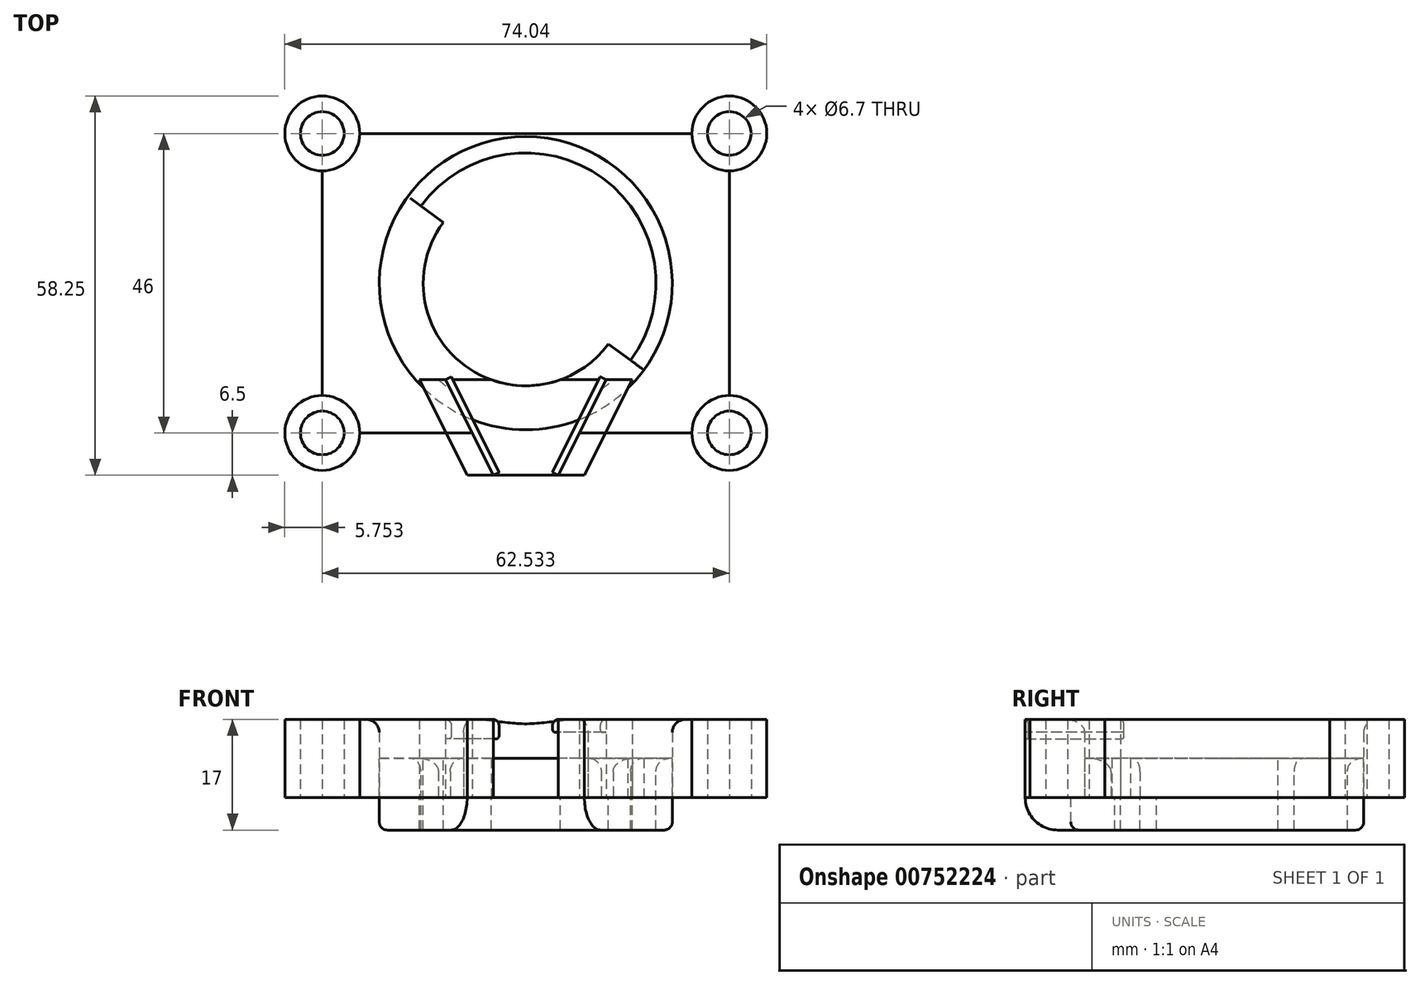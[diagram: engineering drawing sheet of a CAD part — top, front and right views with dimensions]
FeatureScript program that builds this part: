
annotation { "Feature Type Name" : "Feature", "Feature Type Description" : "" }
export const myFeature = defineFeature(function(context is Context, id is Id, definition is map)
    precondition{}
    {
        {
            var Q0;
            Q0=qCreatedBy(makeId("Top.planeOp"),FACE);
            var sketch = newSketch(context, id + "F0", { "sketchPlane" : qUnion([Q0])});
            skCircle(sketch, "E0", {"center": v(-31.27, 23) * mm, "radius": 5.75 * mm});
            skCircle(sketch, "E1", {"center": v(31.27, -23) * mm, "radius": 5.75 * mm});
            skCircle(sketch, "E2", {"center": v(31.27, -23) * mm, "radius": 3.35 * mm});
            skCircle(sketch, "E3", {"center": v(-31.27, 23) * mm, "radius": 3.35 * mm});
            skLineSegment(sketch, "E4", {"start": v(-31.27, 23) * mm, "end": v(31.27, -23) * mm});
            skCircle(sketch, "E5", {"center": v(0, 0) * mm, "radius": 20 * mm});
            skCircle(sketch, "E6", {"center": v(0, 0) * mm, "radius": 15.75 * mm});
            skLineSegment(sketch, "E7", {"start": v(-31.27, 23) * mm, "end": v(-31.27, -23) * mm});
            skLineSegment(sketch, "E8", {"start": v(-31.27, -23) * mm, "end": v(31.27, -23) * mm});
            skCircle(sketch, "E9", {"center": v(-31.27, -23) * mm, "radius": 5.75 * mm});
            skCircle(sketch, "E10", {"center": v(-31.27, -23) * mm, "radius": 3.35 * mm});
            skLineSegment(sketch, "E11", {"start": v(-31.27, 23) * mm, "end": v(31.27, 23) * mm});
            skCircle(sketch, "E12", {"center": v(31.27, 23) * mm, "radius": 5.75 * mm});
            skCircle(sketch, "E13", {"center": v(31.27, 23) * mm, "radius": 3.35 * mm});
            skLineSegment(sketch, "E14", {"start": v(31.27, -23) * mm, "end": v(31.27, 23) * mm});
            skLineSegment(sketch, "E15", {"start": v(0, 0) * mm, "end": v(0, -29.5) * mm});
            skLineSegment(sketch, "E16", {"start": v(-5, -29.5) * mm, "end": v(5, -29.5) * mm});
            skLineSegment(sketch, "E17", {"start": v(-5, -29.5) * mm, "end": v(-9, -29.5) * mm});
            skLineSegment(sketch, "E18", {"start": v(5, -29.5) * mm, "end": v(9, -29.5) * mm});
            skLineSegment(sketch, "E19", {"start": v(-5, -29.5) * mm, "end": v(-12.33, -14.82) * mm});
            skLineSegment(sketch, "E20", {"start": v(-12.33, -14.82) * mm, "end": v(12.33, -14.82) * mm});
            skLineSegment(sketch, "E21", {"start": v(12.33, -14.82) * mm, "end": v(5, -29.5) * mm});
            skLineSegment(sketch, "E22", {"start": v(-12.33, -14.82) * mm, "end": v(-16.33, -14.82) * mm});
            skLineSegment(sketch, "E23", {"start": v(-16.33, -14.82) * mm, "end": v(-9, -29.5) * mm});
            skLineSegment(sketch, "E24", {"start": v(9, -29.5) * mm, "end": v(16.32, -14.82) * mm});
            skLineSegment(sketch, "E25", {"start": v(16.32, -14.82) * mm, "end": v(12.33, -14.82) * mm});
            skCircle(sketch, "E26", {"center": v(0, 0) * mm, "radius": 22.5 * mm});
            skSolve(sketch);
        }
        {
            var Q0;
            {var subQ0=sQuery(id+"F0.wireOp",EDGE,"E9");var subQ1=sQuery(id+"F0.wireOp",EDGE,"E7");var subQ2=makeQuery(id+"F0.imprint","INTERSECT",VERTEX,{"derivedFrom":[subQ1,subQ0]});Q0=makeQuery(id+"F0.imprint","IMPRINT",FACE,{"disambiguationData":[TD([[makeQuery(id+"F0.imprint","IMPRINT",EDGE,{"disambiguationData":[TD([[subQ2,-1.0]])],"derivedFrom":subQ1}),-1.0]])]});}
            var Q1;
            {var subQ0=sQuery(id+"F0.wireOp",EDGE,"E12");var subQ1=sQuery(id+"F0.wireOp",EDGE,"E11");var subQ2=makeQuery(id+"F0.imprint","INTERSECT",VERTEX,{"derivedFrom":[subQ1,subQ0]});Q1=makeQuery(id+"F0.imprint","IMPRINT",FACE,{"disambiguationData":[TD([[makeQuery(id+"F0.imprint","IMPRINT",EDGE,{"disambiguationData":[TD([[subQ2,-1.0]])],"derivedFrom":subQ1}),1.0]])]});}
            var Q2;
            {var subQ0=sQuery(id+"F0.wireOp",EDGE,"E7");var subQ1=sQuery(id+"F0.wireOp",EDGE,"E0");var subQ2=makeQuery(id+"F0.imprint","INTERSECT",VERTEX,{"derivedFrom":[subQ1,subQ0]});Q2=makeQuery(id+"F0.imprint","IMPRINT",FACE,{"disambiguationData":[TD([[makeQuery(id+"F0.imprint","IMPRINT",EDGE,{"disambiguationData":[TD([[subQ2,1.0]])],"derivedFrom":subQ1}),1.0]])]});}
            var Q3;
            {var subQ0=sQuery(id+"F0.wireOp",EDGE,"E14");var subQ1=sQuery(id+"F0.wireOp",EDGE,"E1");var subQ2=makeQuery(id+"F0.imprint","INTERSECT",VERTEX,{"derivedFrom":[subQ1,subQ0]});Q3=makeQuery(id+"F0.imprint","IMPRINT",FACE,{"disambiguationData":[TD([[makeQuery(id+"F0.imprint","IMPRINT",EDGE,{"disambiguationData":[TD([[subQ2,1.0]])],"derivedFrom":subQ1}),1.0]])]});}
            var Q4;
            {var subQ0=sQuery(id+"F0.wireOp",EDGE,"E9");var subQ1=sQuery(id+"F0.wireOp",EDGE,"E7");var subQ2=makeQuery(id+"F0.imprint","INTERSECT",VERTEX,{"derivedFrom":[subQ1,subQ0]});Q4=makeQuery(id+"F0.imprint","IMPRINT",FACE,{"disambiguationData":[TD([[makeQuery(id+"F0.imprint","IMPRINT",EDGE,{"disambiguationData":[TD([[subQ2,-1.0]])],"derivedFrom":subQ1}),1.0]])]});}
            var Q5;
            {var subQ0=sQuery(id+"F0.wireOp",EDGE,"E12");var subQ1=sQuery(id+"F0.wireOp",EDGE,"E11");var subQ2=makeQuery(id+"F0.imprint","INTERSECT",VERTEX,{"derivedFrom":[subQ1,subQ0]});Q5=makeQuery(id+"F0.imprint","IMPRINT",FACE,{"disambiguationData":[TD([[makeQuery(id+"F0.imprint","IMPRINT",EDGE,{"disambiguationData":[TD([[subQ2,-1.0]])],"derivedFrom":subQ1}),-1.0]])]});}
            var Q6;
            {var subQ0=sQuery(id+"F0.wireOp",EDGE,"E7");var subQ1=sQuery(id+"F0.wireOp",EDGE,"E0");var subQ2=makeQuery(id+"F0.imprint","INTERSECT",VERTEX,{"derivedFrom":[subQ1,subQ0]});Q6=makeQuery(id+"F0.imprint","IMPRINT",FACE,{"disambiguationData":[TD([[makeQuery(id+"F0.imprint","IMPRINT",EDGE,{"disambiguationData":[TD([[subQ2,-1.0]])],"derivedFrom":subQ1}),1.0]])]});}
            var Q7;
            {var subQ0=sQuery(id+"F0.wireOp",EDGE,"E11");var subQ1=sQuery(id+"F0.wireOp",EDGE,"E0");var subQ2=makeQuery(id+"F0.imprint","INTERSECT",VERTEX,{"derivedFrom":[subQ1,subQ0]});Q7=makeQuery(id+"F0.imprint","IMPRINT",FACE,{"disambiguationData":[TD([[makeQuery(id+"F0.imprint","IMPRINT",EDGE,{"disambiguationData":[TD([[subQ2,1.0]])],"derivedFrom":subQ1}),1.0]])]});}
            var Q8;
            {var subQ0=sQuery(id+"F0.wireOp",EDGE,"E14");var subQ1=sQuery(id+"F0.wireOp",EDGE,"E1");var subQ2=makeQuery(id+"F0.imprint","INTERSECT",VERTEX,{"derivedFrom":[subQ1,subQ0]});Q8=makeQuery(id+"F0.imprint","IMPRINT",FACE,{"disambiguationData":[TD([[makeQuery(id+"F0.imprint","IMPRINT",EDGE,{"disambiguationData":[TD([[subQ2,-1.0]])],"derivedFrom":subQ1}),1.0]])]});}
            var Q9;
            {var subQ0=sQuery(id+"F0.wireOp",EDGE,"E8");var subQ1=sQuery(id+"F0.wireOp",EDGE,"E1");var subQ2=makeQuery(id+"F0.imprint","INTERSECT",VERTEX,{"derivedFrom":[subQ1,subQ0]});Q9=makeQuery(id+"F0.imprint","IMPRINT",FACE,{"disambiguationData":[TD([[makeQuery(id+"F0.imprint","IMPRINT",EDGE,{"disambiguationData":[TD([[subQ2,1.0]])],"derivedFrom":subQ1}),1.0]])]});}
            extrude(context, id + "F1", {"entities" : qUnion([Q0, Q1, Q2, Q3, Q4, Q5, Q6, Q7, Q8, Q9]), "depth" : 12 * mm, "offsetDistance" : 25 * mm});
        }
        {
            var Q0;
            {var subQ5=sQuery(id+"F0.wireOp",EDGE,"E15");var subQ6=sQuery(id+"F0.wireOp",EDGE,"E5");var subQ7=makeQuery(id+"F0.imprint","INTERSECT",VERTEX,{"derivedFrom":[subQ6,subQ5]});Q0=makeQuery(id+"F0.imprint","IMPRINT",FACE,{"disambiguationData":[TD([[makeQuery(id+"F0.imprint","IMPRINT",EDGE,{"disambiguationData":[TD([[subQ7,-1.0]])],"derivedFrom":subQ6}),1.0]])]});}
            var Q1;
            {var subQ3=sQuery(id+"F0.wireOp",EDGE,"E6");var subQ5=sQuery(id+"F0.wireOp",EDGE,"E4");var subQ6=makeQuery(id+"F0.imprint","INTERSECT",VERTEX,{"disambiguationData":[OD(1.0)],"derivedFrom":[subQ5,subQ3]});Q1=makeQuery(id+"F0.imprint","IMPRINT",FACE,{"disambiguationData":[TD([[makeQuery(id+"F0.imprint","IMPRINT",EDGE,{"disambiguationData":[TD([[subQ6,-1.0]])],"derivedFrom":subQ5}),-1.0]])]});}
            var Q2;
            {var subQ0=sQuery(id+"F0.wireOp",EDGE,"E21");var subQ1=sQuery(id+"F0.wireOp",EDGE,"E5");var subQ2=makeQuery(id+"F0.imprint","INTERSECT",VERTEX,{"derivedFrom":[subQ1,subQ0]});Q2=makeQuery(id+"F0.imprint","IMPRINT",FACE,{"disambiguationData":[TD([[makeQuery(id+"F0.imprint","IMPRINT",EDGE,{"disambiguationData":[TD([[subQ2,-1.0]])],"derivedFrom":subQ1}),1.0]])]});}
            var Q3;
            {var subQ0=sQuery(id+"F0.wireOp",EDGE,"E5");var subQ1=sQuery(id+"F0.wireOp",EDGE,"E4");var subQ2=makeQuery(id+"F0.imprint","INTERSECT",VERTEX,{"disambiguationData":[OD(0.0)],"derivedFrom":[subQ1,subQ0]});Q3=makeQuery(id+"F0.imprint","IMPRINT",FACE,{"disambiguationData":[TD([[makeQuery(id+"F0.imprint","IMPRINT",EDGE,{"disambiguationData":[TD([[subQ2,-1.0]])],"derivedFrom":subQ1}),1.0]])]});}
            var Q4;
            {var subQ5=sQuery(id+"F0.wireOp",EDGE,"E5");var subQ6=sQuery(id+"F0.wireOp",EDGE,"E4");var subQ7=makeQuery(id+"F0.imprint","INTERSECT",VERTEX,{"disambiguationData":[OD(0.0)],"derivedFrom":[subQ6,subQ5]});Q4=makeQuery(id+"F0.imprint","IMPRINT",FACE,{"disambiguationData":[TD([[makeQuery(id+"F0.imprint","IMPRINT",EDGE,{"disambiguationData":[TD([[subQ7,-1.0]])],"derivedFrom":subQ6}),-1.0]])]});}
            var Q5;
            {var subQ1=sQuery(id+"F0.wireOp",EDGE,"E19");var subQ3=sQuery(id+"F0.wireOp",EDGE,"E5");var subQ4=makeQuery(id+"F0.imprint","INTERSECT",VERTEX,{"derivedFrom":[subQ3,subQ1]});Q5=makeQuery(id+"F0.imprint","IMPRINT",FACE,{"disambiguationData":[TD([[makeQuery(id+"F0.imprint","IMPRINT",EDGE,{"disambiguationData":[TD([[subQ4,-1.0]])],"derivedFrom":subQ3}),1.0]])]});}
            var Q6;
            {var subQ0=sQuery(id+"F0.wireOp",EDGE,"E22");var subQ1=sQuery(id+"F0.wireOp",EDGE,"E5");var subQ2=makeQuery(id+"F0.imprint","INTERSECT",VERTEX,{"derivedFrom":[subQ1,subQ0]});Q6=makeQuery(id+"F0.imprint","IMPRINT",FACE,{"disambiguationData":[TD([[makeQuery(id+"F0.imprint","IMPRINT",EDGE,{"disambiguationData":[TD([[subQ2,-1.0]])],"derivedFrom":subQ1}),1.0]])]});}
            extrude(context, id + "F2", {"entities" : qUnion([Q0, Q1, Q2, Q3, Q4, Q5, Q6]), "depth" : -5 * mm, "offsetDistance" : 25 * mm});
        }
        {
            var Q0;
            {var subQ1=sQuery(id+"F0.wireOp",EDGE,"E22");var subQ5=sQuery(id+"F0.wireOp",EDGE,"E5");var subQ6=makeQuery(id+"F0.imprint","INTERSECT",VERTEX,{"derivedFrom":[subQ5,subQ1]});Q0=makeQuery(id+"F0.imprint","IMPRINT",FACE,{"disambiguationData":[TD([[makeQuery(id+"F0.imprint","IMPRINT",EDGE,{"disambiguationData":[TD([[subQ6,-1.0]])],"derivedFrom":subQ5}),-1.0]])]});}
            var Q1;
            {var subQ3=sQuery(id+"F0.wireOp",EDGE,"E26");var subQ7=sQuery(id+"F0.wireOp",EDGE,"E4");var subQ8=makeQuery(id+"F0.imprint","INTERSECT",VERTEX,{"disambiguationData":[OD(0.0)],"derivedFrom":[subQ7,subQ3]});Q1=makeQuery(id+"F0.imprint","IMPRINT",FACE,{"disambiguationData":[TD([[makeQuery(id+"F0.imprint","IMPRINT",EDGE,{"disambiguationData":[TD([[subQ8,-1.0]])],"derivedFrom":subQ7}),-1.0]])]});}
            var Q2;
            {var subQ0=sQuery(id+"F0.wireOp",EDGE,"E26");var subQ1=sQuery(id+"F0.wireOp",EDGE,"E4");var subQ2=makeQuery(id+"F0.imprint","INTERSECT",VERTEX,{"disambiguationData":[OD(0.0)],"derivedFrom":[subQ1,subQ0]});Q2=makeQuery(id+"F0.imprint","IMPRINT",FACE,{"disambiguationData":[TD([[makeQuery(id+"F0.imprint","IMPRINT",EDGE,{"disambiguationData":[TD([[subQ2,-1.0]])],"derivedFrom":subQ1}),1.0]])]});}
            var Q3;
            {var subQ5=sQuery(id+"F0.wireOp",EDGE,"E5");var subQ7=sQuery(id+"F0.wireOp",EDGE,"E4");var subQ8=makeQuery(id+"F0.imprint","INTERSECT",VERTEX,{"disambiguationData":[OD(1.0)],"derivedFrom":[subQ7,subQ5]});Q3=makeQuery(id+"F0.imprint","IMPRINT",FACE,{"disambiguationData":[TD([[makeQuery(id+"F0.imprint","IMPRINT",EDGE,{"disambiguationData":[TD([[subQ8,-1.0]])],"derivedFrom":subQ7}),-1.0]])]});}
            var Q4;
            {var subQ3=sQuery(id+"F0.wireOp",EDGE,"E5");var subQ5=sQuery(id+"F0.wireOp",EDGE,"E21");var subQ6=makeQuery(id+"F0.imprint","INTERSECT",VERTEX,{"derivedFrom":[subQ3,subQ5]});Q4=makeQuery(id+"F0.imprint","IMPRINT",FACE,{"disambiguationData":[TD([[makeQuery(id+"F0.imprint","IMPRINT",EDGE,{"disambiguationData":[TD([[subQ6,-1.0]])],"derivedFrom":subQ3}),-1.0]])]});}
            var Q5;
            {var subQ0=sQuery(id+"F0.wireOp",EDGE,"E15");var subQ1=sQuery(id+"F0.wireOp",EDGE,"E5");var subQ2=makeQuery(id+"F0.imprint","INTERSECT",VERTEX,{"derivedFrom":[subQ1,subQ0]});Q5=makeQuery(id+"F0.imprint","IMPRINT",FACE,{"disambiguationData":[TD([[makeQuery(id+"F0.imprint","IMPRINT",EDGE,{"disambiguationData":[TD([[subQ2,-1.0]])],"derivedFrom":subQ1}),-1.0]])]});}
            var Q6;
            {var subQ0=sQuery(id+"F0.wireOp",EDGE,"E19");var subQ1=sQuery(id+"F0.wireOp",EDGE,"E5");var subQ2=makeQuery(id+"F0.imprint","INTERSECT",VERTEX,{"derivedFrom":[subQ1,subQ0]});Q6=makeQuery(id+"F0.imprint","IMPRINT",FACE,{"disambiguationData":[TD([[makeQuery(id+"F0.imprint","IMPRINT",EDGE,{"disambiguationData":[TD([[subQ2,-1.0]])],"derivedFrom":subQ1}),-1.0]])]});}
            extrude(context, id + "F3", {"entities" : qUnion([Q0, Q1, Q2, Q3, Q4, Q5, Q6]), "operationType" : NewBodyOperationType.ADD, "depth" : -5 * mm, "offsetDistance" : 25 * mm});
        }
        {
            var Q0;
            {var subQ3=sQuery(id+"F0.wireOp",EDGE,"E26");var subQ7=sQuery(id+"F0.wireOp",EDGE,"E4");var subQ8=makeQuery(id+"F0.imprint","INTERSECT",VERTEX,{"disambiguationData":[OD(0.0)],"derivedFrom":[subQ7,subQ3]});Q0=makeQuery(id+"F0.imprint","IMPRINT",FACE,{"disambiguationData":[TD([[makeQuery(id+"F0.imprint","IMPRINT",EDGE,{"disambiguationData":[TD([[subQ8,-1.0]])],"derivedFrom":subQ7}),-1.0]])]});}
            var Q1;
            {var subQ1=sQuery(id+"F0.wireOp",EDGE,"E22");var subQ5=sQuery(id+"F0.wireOp",EDGE,"E5");var subQ6=makeQuery(id+"F0.imprint","INTERSECT",VERTEX,{"derivedFrom":[subQ5,subQ1]});Q1=makeQuery(id+"F0.imprint","IMPRINT",FACE,{"disambiguationData":[TD([[makeQuery(id+"F0.imprint","IMPRINT",EDGE,{"disambiguationData":[TD([[subQ6,-1.0]])],"derivedFrom":subQ5}),-1.0]])]});}
            var Q2;
            {var subQ3=sQuery(id+"F0.wireOp",EDGE,"E5");var subQ5=sQuery(id+"F0.wireOp",EDGE,"E21");var subQ6=makeQuery(id+"F0.imprint","INTERSECT",VERTEX,{"derivedFrom":[subQ3,subQ5]});Q2=makeQuery(id+"F0.imprint","IMPRINT",FACE,{"disambiguationData":[TD([[makeQuery(id+"F0.imprint","IMPRINT",EDGE,{"disambiguationData":[TD([[subQ6,-1.0]])],"derivedFrom":subQ3}),-1.0]])]});}
            var Q3;
            {var subQ5=sQuery(id+"F0.wireOp",EDGE,"E5");var subQ7=sQuery(id+"F0.wireOp",EDGE,"E4");var subQ8=makeQuery(id+"F0.imprint","INTERSECT",VERTEX,{"disambiguationData":[OD(1.0)],"derivedFrom":[subQ7,subQ5]});Q3=makeQuery(id+"F0.imprint","IMPRINT",FACE,{"disambiguationData":[TD([[makeQuery(id+"F0.imprint","IMPRINT",EDGE,{"disambiguationData":[TD([[subQ8,-1.0]])],"derivedFrom":subQ7}),-1.0]])]});}
            var Q4;
            {var subQ0=sQuery(id+"F0.wireOp",EDGE,"E26");var subQ1=sQuery(id+"F0.wireOp",EDGE,"E4");var subQ2=makeQuery(id+"F0.imprint","INTERSECT",VERTEX,{"disambiguationData":[OD(0.0)],"derivedFrom":[subQ1,subQ0]});Q4=makeQuery(id+"F0.imprint","IMPRINT",FACE,{"disambiguationData":[TD([[makeQuery(id+"F0.imprint","IMPRINT",EDGE,{"disambiguationData":[TD([[subQ2,-1.0]])],"derivedFrom":subQ1}),1.0]])]});}
            extrude(context, id + "F4", {"entities" : qUnion([Q0, Q1, Q2, Q3, Q4]), "operationType" : NewBodyOperationType.ADD, "depth" : 6 * mm, "offsetDistance" : 25 * mm});
        }
        {
            var Q0;
            {var subQ5=sQuery(id+"F0.wireOp",EDGE,"E7");var subQ6=sQuery(id+"F0.wireOp",EDGE,"E0");var subQ7=makeQuery(id+"F0.imprint","INTERSECT",VERTEX,{"derivedFrom":[subQ6,subQ5]});Q0=makeQuery(id+"F0.imprint","IMPRINT",FACE,{"disambiguationData":[TD([[makeQuery(id+"F0.imprint","IMPRINT",EDGE,{"disambiguationData":[TD([[subQ7,-1.0]])],"derivedFrom":subQ6}),-1.0]])]});}
            var Q1;
            {var subQ5=sQuery(id+"F0.wireOp",EDGE,"E0");var subQ10=sQuery(id+"F0.wireOp",EDGE,"E11");var subQ11=makeQuery(id+"F0.imprint","INTERSECT",VERTEX,{"derivedFrom":[subQ5,subQ10]});Q1=makeQuery(id+"F0.imprint","IMPRINT",FACE,{"disambiguationData":[TD([[makeQuery(id+"F0.imprint","IMPRINT",EDGE,{"disambiguationData":[TD([[subQ11,1.0]])],"derivedFrom":subQ5}),-1.0]])]});}
            var Q2;
            {var subQ1=sQuery(id+"F0.wireOp",EDGE,"E8");var subQ5=sQuery(id+"F0.wireOp",EDGE,"E1");var subQ6=makeQuery(id+"F0.imprint","INTERSECT",VERTEX,{"derivedFrom":[subQ5,subQ1]});Q2=makeQuery(id+"F0.imprint","IMPRINT",FACE,{"disambiguationData":[TD([[makeQuery(id+"F0.imprint","IMPRINT",EDGE,{"disambiguationData":[TD([[subQ6,1.0]])],"derivedFrom":subQ5}),-1.0]])]});}
            var Q3;
            {var subQ0=sQuery(id+"F0.wireOp",EDGE,"E23");var subQ1=sQuery(id+"F0.wireOp",EDGE,"E8");var subQ2=makeQuery(id+"F0.imprint","INTERSECT",VERTEX,{"derivedFrom":[subQ1,subQ0]});Q3=makeQuery(id+"F0.imprint","IMPRINT",FACE,{"disambiguationData":[TD([[makeQuery(id+"F0.imprint","IMPRINT",EDGE,{"disambiguationData":[TD([[subQ2,-1.0]])],"derivedFrom":subQ1}),1.0]])]});}
            var Q4;
            {var subQ0=sQuery(id+"F0.wireOp",EDGE,"E24");var subQ1=sQuery(id+"F0.wireOp",EDGE,"E8");var subQ2=makeQuery(id+"F0.imprint","INTERSECT",VERTEX,{"derivedFrom":[subQ1,subQ0]});Q4=makeQuery(id+"F0.imprint","IMPRINT",FACE,{"disambiguationData":[TD([[makeQuery(id+"F0.imprint","IMPRINT",EDGE,{"disambiguationData":[TD([[subQ2,1.0]])],"derivedFrom":subQ1}),1.0]])]});}
            extrude(context, id + "F5", {"entities" : qUnion([Q0, Q1, Q2, Q3, Q4]), "depth" : 12 * mm, "offsetDistance" : 25 * mm});
        }
        {
            var Q0;
            Q0=makeQuery(id+"F4.opExtrude","CAP_EDGE",EDGE,{"disambiguationData":[OSD([sQuery(id+"F0.wireOp",EDGE,"E5")])],"isStart":false});
            fillet(context, id + "F6", {"entities" : qUnion([Q0]), "radius" : 2 * mm, "tangentPropagation" : true, "allowEdgeOverflow" : false});
        }
        {
            var Q0;
            Q0=makeQuery(id+"F5.opExtrude","CAP_EDGE",EDGE,{"disambiguationData":[OSD([sQuery(id+"F0.wireOp",EDGE,"E26")])],"isStart":false});
            fillet(context, id + "F7", {"entities" : qUnion([Q0]), "radius" : 2 * mm, "tangentPropagation" : true, "allowEdgeOverflow" : false});
        }
        {
            var Q0;
            {var subQ5=sQuery(id+"F0.wireOp",EDGE,"E18");Q0=makeQuery(id+"F0.imprint","IMPRINT",FACE,{"disambiguationData":[TD([[makeQuery(id+"F0.imprint","IMPRINT",EDGE,{"derivedFrom":subQ5}),1.0]])]});}
            var Q1;
            {var subQ0=sQuery(id+"F0.wireOp",EDGE,"E24");var subQ1=sQuery(id+"F0.wireOp",EDGE,"E8");var subQ2=makeQuery(id+"F0.imprint","INTERSECT",VERTEX,{"derivedFrom":[subQ1,subQ0]});Q1=makeQuery(id+"F0.imprint","IMPRINT",FACE,{"disambiguationData":[TD([[makeQuery(id+"F0.imprint","IMPRINT",EDGE,{"disambiguationData":[TD([[subQ2,1.0]])],"derivedFrom":subQ1}),1.0]])]});}
            var Q2;
            {var subQ3=sQuery(id+"F0.wireOp",EDGE,"E5");var subQ5=sQuery(id+"F0.wireOp",EDGE,"E21");var subQ6=makeQuery(id+"F0.imprint","INTERSECT",VERTEX,{"derivedFrom":[subQ3,subQ5]});Q2=makeQuery(id+"F0.imprint","IMPRINT",FACE,{"disambiguationData":[TD([[makeQuery(id+"F0.imprint","IMPRINT",EDGE,{"disambiguationData":[TD([[subQ6,-1.0]])],"derivedFrom":subQ3}),-1.0]])]});}
            var Q3;
            {var subQ0=sQuery(id+"F0.wireOp",EDGE,"E21");var subQ1=sQuery(id+"F0.wireOp",EDGE,"E5");var subQ2=makeQuery(id+"F0.imprint","INTERSECT",VERTEX,{"derivedFrom":[subQ1,subQ0]});Q3=makeQuery(id+"F0.imprint","IMPRINT",FACE,{"disambiguationData":[TD([[makeQuery(id+"F0.imprint","IMPRINT",EDGE,{"disambiguationData":[TD([[subQ2,-1.0]])],"derivedFrom":subQ1}),1.0]])]});}
            var Q4;
            {var subQ0=sQuery(id+"F0.wireOp",EDGE,"E22");var subQ1=sQuery(id+"F0.wireOp",EDGE,"E5");var subQ2=makeQuery(id+"F0.imprint","INTERSECT",VERTEX,{"derivedFrom":[subQ1,subQ0]});Q4=makeQuery(id+"F0.imprint","IMPRINT",FACE,{"disambiguationData":[TD([[makeQuery(id+"F0.imprint","IMPRINT",EDGE,{"disambiguationData":[TD([[subQ2,-1.0]])],"derivedFrom":subQ1}),1.0]])]});}
            var Q5;
            {var subQ1=sQuery(id+"F0.wireOp",EDGE,"E22");var subQ5=sQuery(id+"F0.wireOp",EDGE,"E5");var subQ6=makeQuery(id+"F0.imprint","INTERSECT",VERTEX,{"derivedFrom":[subQ5,subQ1]});Q5=makeQuery(id+"F0.imprint","IMPRINT",FACE,{"disambiguationData":[TD([[makeQuery(id+"F0.imprint","IMPRINT",EDGE,{"disambiguationData":[TD([[subQ6,-1.0]])],"derivedFrom":subQ5}),-1.0]])]});}
            var Q6;
            {var subQ0=sQuery(id+"F0.wireOp",EDGE,"E23");var subQ1=sQuery(id+"F0.wireOp",EDGE,"E8");var subQ2=makeQuery(id+"F0.imprint","INTERSECT",VERTEX,{"derivedFrom":[subQ1,subQ0]});Q6=makeQuery(id+"F0.imprint","IMPRINT",FACE,{"disambiguationData":[TD([[makeQuery(id+"F0.imprint","IMPRINT",EDGE,{"disambiguationData":[TD([[subQ2,-1.0]])],"derivedFrom":subQ1}),1.0]])]});}
            var Q7;
            {var subQ5=sQuery(id+"F0.wireOp",EDGE,"E17");Q7=makeQuery(id+"F0.imprint","IMPRINT",FACE,{"disambiguationData":[TD([[makeQuery(id+"F0.imprint","IMPRINT",EDGE,{"derivedFrom":subQ5}),-1.0]])]});}
            var Q8;
            {var subQ0=sQuery(id+"F0.wireOp",EDGE,"E19");var subQ1=sQuery(id+"F0.wireOp",EDGE,"E8");var subQ2=makeQuery(id+"F0.imprint","INTERSECT",VERTEX,{"derivedFrom":[subQ1,subQ0]});Q8=makeQuery(id+"F0.imprint","IMPRINT",FACE,{"disambiguationData":[TD([[makeQuery(id+"F0.imprint","IMPRINT",EDGE,{"disambiguationData":[TD([[subQ2,-1.0]])],"derivedFrom":subQ1}),-1.0]])]});}
            var Q9;
            {var subQ0=sQuery(id+"F0.wireOp",EDGE,"E19");var subQ1=sQuery(id+"F0.wireOp",EDGE,"E8");var subQ2=makeQuery(id+"F0.imprint","INTERSECT",VERTEX,{"derivedFrom":[subQ1,subQ0]});Q9=makeQuery(id+"F0.imprint","IMPRINT",FACE,{"disambiguationData":[TD([[makeQuery(id+"F0.imprint","IMPRINT",EDGE,{"disambiguationData":[TD([[subQ2,-1.0]])],"derivedFrom":subQ1}),1.0]])]});}
            var Q10;
            {var subQ0=sQuery(id+"F0.wireOp",EDGE,"E15");var subQ1=sQuery(id+"F0.wireOp",EDGE,"E8");var subQ2=makeQuery(id+"F0.imprint","INTERSECT",VERTEX,{"derivedFrom":[subQ1,subQ0]});Q10=makeQuery(id+"F0.imprint","IMPRINT",FACE,{"disambiguationData":[TD([[makeQuery(id+"F0.imprint","IMPRINT",EDGE,{"disambiguationData":[TD([[subQ2,-1.0]])],"derivedFrom":subQ1}),-1.0]])]});}
            var Q11;
            {var subQ0=sQuery(id+"F0.wireOp",EDGE,"E15");var subQ1=sQuery(id+"F0.wireOp",EDGE,"E8");var subQ2=makeQuery(id+"F0.imprint","INTERSECT",VERTEX,{"derivedFrom":[subQ1,subQ0]});Q11=makeQuery(id+"F0.imprint","IMPRINT",FACE,{"disambiguationData":[TD([[makeQuery(id+"F0.imprint","IMPRINT",EDGE,{"disambiguationData":[TD([[subQ2,-1.0]])],"derivedFrom":subQ1}),1.0]])]});}
            var Q12;
            {var subQ0=sQuery(id+"F0.wireOp",EDGE,"E15");var subQ1=sQuery(id+"F0.wireOp",EDGE,"E5");var subQ2=makeQuery(id+"F0.imprint","INTERSECT",VERTEX,{"derivedFrom":[subQ1,subQ0]});Q12=makeQuery(id+"F0.imprint","IMPRINT",FACE,{"disambiguationData":[TD([[makeQuery(id+"F0.imprint","IMPRINT",EDGE,{"disambiguationData":[TD([[subQ2,-1.0]])],"derivedFrom":subQ1}),-1.0]])]});}
            var Q13;
            {var subQ0=sQuery(id+"F0.wireOp",EDGE,"E19");var subQ1=sQuery(id+"F0.wireOp",EDGE,"E5");var subQ2=makeQuery(id+"F0.imprint","INTERSECT",VERTEX,{"derivedFrom":[subQ1,subQ0]});Q13=makeQuery(id+"F0.imprint","IMPRINT",FACE,{"disambiguationData":[TD([[makeQuery(id+"F0.imprint","IMPRINT",EDGE,{"disambiguationData":[TD([[subQ2,-1.0]])],"derivedFrom":subQ1}),-1.0]])]});}
            var Q14;
            {var subQ1=sQuery(id+"F0.wireOp",EDGE,"E19");var subQ3=sQuery(id+"F0.wireOp",EDGE,"E5");var subQ4=makeQuery(id+"F0.imprint","INTERSECT",VERTEX,{"derivedFrom":[subQ3,subQ1]});Q14=makeQuery(id+"F0.imprint","IMPRINT",FACE,{"disambiguationData":[TD([[makeQuery(id+"F0.imprint","IMPRINT",EDGE,{"disambiguationData":[TD([[subQ4,-1.0]])],"derivedFrom":subQ3}),1.0]])]});}
            var Q15;
            {var subQ5=sQuery(id+"F0.wireOp",EDGE,"E15");var subQ6=sQuery(id+"F0.wireOp",EDGE,"E5");var subQ7=makeQuery(id+"F0.imprint","INTERSECT",VERTEX,{"derivedFrom":[subQ6,subQ5]});Q15=makeQuery(id+"F0.imprint","IMPRINT",FACE,{"disambiguationData":[TD([[makeQuery(id+"F0.imprint","IMPRINT",EDGE,{"disambiguationData":[TD([[subQ7,-1.0]])],"derivedFrom":subQ6}),1.0]])]});}
            extrude(context, id + "F8", {"entities" : qUnion([Q0, Q1, Q2, Q3, Q4, Q5, Q6, Q7, Q8, Q9, Q10, Q11, Q12, Q13, Q14, Q15]), "depth" : -5 * mm, "offsetDistance" : 25 * mm});
        }
        {
            var Q0;
            {var subQ1=sQuery(id+"F0.wireOp",EDGE,"E22");var subQ5=sQuery(id+"F0.wireOp",EDGE,"E5");var subQ6=makeQuery(id+"F0.imprint","INTERSECT",VERTEX,{"derivedFrom":[subQ5,subQ1]});Q0=makeQuery(id+"F0.imprint","IMPRINT",FACE,{"disambiguationData":[TD([[makeQuery(id+"F0.imprint","IMPRINT",EDGE,{"disambiguationData":[TD([[subQ6,-1.0]])],"derivedFrom":subQ5}),-1.0]])]});}
            var Q1;
            {var subQ0=sQuery(id+"F0.wireOp",EDGE,"E22");var subQ1=sQuery(id+"F0.wireOp",EDGE,"E5");var subQ2=makeQuery(id+"F0.imprint","INTERSECT",VERTEX,{"derivedFrom":[subQ1,subQ0]});Q1=makeQuery(id+"F0.imprint","IMPRINT",FACE,{"disambiguationData":[TD([[makeQuery(id+"F0.imprint","IMPRINT",EDGE,{"disambiguationData":[TD([[subQ2,-1.0]])],"derivedFrom":subQ1}),1.0]])]});}
            var Q2;
            {var subQ0=sQuery(id+"F0.wireOp",EDGE,"E23");var subQ1=sQuery(id+"F0.wireOp",EDGE,"E8");var subQ2=makeQuery(id+"F0.imprint","INTERSECT",VERTEX,{"derivedFrom":[subQ1,subQ0]});Q2=makeQuery(id+"F0.imprint","IMPRINT",FACE,{"disambiguationData":[TD([[makeQuery(id+"F0.imprint","IMPRINT",EDGE,{"disambiguationData":[TD([[subQ2,-1.0]])],"derivedFrom":subQ1}),1.0]])]});}
            var Q3;
            {var subQ5=sQuery(id+"F0.wireOp",EDGE,"E17");Q3=makeQuery(id+"F0.imprint","IMPRINT",FACE,{"disambiguationData":[TD([[makeQuery(id+"F0.imprint","IMPRINT",EDGE,{"derivedFrom":subQ5}),-1.0]])]});}
            var Q4;
            {var subQ5=sQuery(id+"F0.wireOp",EDGE,"E18");Q4=makeQuery(id+"F0.imprint","IMPRINT",FACE,{"disambiguationData":[TD([[makeQuery(id+"F0.imprint","IMPRINT",EDGE,{"derivedFrom":subQ5}),1.0]])]});}
            var Q5;
            {var subQ0=sQuery(id+"F0.wireOp",EDGE,"E24");var subQ1=sQuery(id+"F0.wireOp",EDGE,"E8");var subQ2=makeQuery(id+"F0.imprint","INTERSECT",VERTEX,{"derivedFrom":[subQ1,subQ0]});Q5=makeQuery(id+"F0.imprint","IMPRINT",FACE,{"disambiguationData":[TD([[makeQuery(id+"F0.imprint","IMPRINT",EDGE,{"disambiguationData":[TD([[subQ2,1.0]])],"derivedFrom":subQ1}),1.0]])]});}
            var Q6;
            {var subQ3=sQuery(id+"F0.wireOp",EDGE,"E5");var subQ5=sQuery(id+"F0.wireOp",EDGE,"E21");var subQ6=makeQuery(id+"F0.imprint","INTERSECT",VERTEX,{"derivedFrom":[subQ3,subQ5]});Q6=makeQuery(id+"F0.imprint","IMPRINT",FACE,{"disambiguationData":[TD([[makeQuery(id+"F0.imprint","IMPRINT",EDGE,{"disambiguationData":[TD([[subQ6,-1.0]])],"derivedFrom":subQ3}),-1.0]])]});}
            var Q7;
            {var subQ0=sQuery(id+"F0.wireOp",EDGE,"E21");var subQ1=sQuery(id+"F0.wireOp",EDGE,"E5");var subQ2=makeQuery(id+"F0.imprint","INTERSECT",VERTEX,{"derivedFrom":[subQ1,subQ0]});Q7=makeQuery(id+"F0.imprint","IMPRINT",FACE,{"disambiguationData":[TD([[makeQuery(id+"F0.imprint","IMPRINT",EDGE,{"disambiguationData":[TD([[subQ2,-1.0]])],"derivedFrom":subQ1}),1.0]])]});}
            extrude(context, id + "F9", {"entities" : qUnion([Q0, Q1, Q2, Q3, Q4, Q5, Q6, Q7]), "depth" : 12 * mm, "offsetDistance" : 25 * mm});
        }
        {
            var Q0;
            Q0=makeQuery(id+"F9.opExtrude","SWEPT_FACE",FACE,{"disambiguationData":[OSD([sQuery(id+"F0.wireOp",EDGE,"E21")])]});
            var sketch = newSketch(context, id + "F10", { "sketchPlane" : qUnion([Q0])});
            skLineSegment(sketch, "E27.bottom", {"start": v(7.76, 12) * mm, "end": v(7.76, 12) * mm});
            skLineSegment(sketch, "E27.top", {"start": v(7.76, 10) * mm, "end": v(7.76, 10) * mm});
            skLineSegment(sketch, "E27.left", {"start": v(7.76, 12) * mm, "end": v(7.76, 10) * mm});
            skLineSegment(sketch, "E27.right", {"start": v(7.76, 12) * mm, "end": v(7.76, 10) * mm});
            skLineSegment(sketch, "E28.bottom", {"start": v(7.76, 12) * mm, "end": v(24.16, 12) * mm});
            skLineSegment(sketch, "E28.top", {"start": v(7.76, 10) * mm, "end": v(24.16, 10) * mm});
            skLineSegment(sketch, "E28.right", {"start": v(24.16, 12) * mm, "end": v(24.16, 10) * mm});
            skSolve(sketch);
        }
        {
            var Q0;
            Q0 = qSketchRegion(id + "F10", true);
            extrude(context, id + "F11", {"entities" : qUnion([Q0]), "depth" : 1 * mm, "offsetDistance" : 25 * mm});
        }
        {
            var Q0;
            Q0=makeQuery(id+"F11.opExtrude","CAP_EDGE",EDGE,{"disambiguationData":[OSD([sQuery(id+"F10.wireOp",EDGE,"E28.bottom")])],"isStart":false});
            fillet(context, id + "F12", {"entities" : qUnion([Q0]), "radius" : 1 * mm, "tangentPropagation" : true, "allowEdgeOverflow" : false});
        }
        {
            var Q0;
            Q0=makeQuery(id+"F11.opExtrude","CAP_EDGE",EDGE,{"disambiguationData":[OSD([sQuery(id+"F10.wireOp",EDGE,"E28.top")])],"isStart":false});
            fillet(context, id + "F13", {"entities" : qUnion([Q0]), "radius" : 0.5 * mm, "tangentPropagation" : true, "allowEdgeOverflow" : false});
        }
        {
            var Q0;
            Q0=makeQuery(id+"F9.opExtrude","SWEPT_FACE",FACE,{"disambiguationData":[OSD([sQuery(id+"F0.wireOp",EDGE,"E19")])]});
            var sketch = newSketch(context, id + "F14", { "sketchPlane" : qUnion([Q0])});
            skLineSegment(sketch, "E29.bottom", {"start": v(-24.16, 12) * mm, "end": v(-7.76, 12) * mm});
            skLineSegment(sketch, "E29.top", {"start": v(-24.16, 9) * mm, "end": v(-7.76, 9) * mm});
            skLineSegment(sketch, "E29.left", {"start": v(-24.16, 12) * mm, "end": v(-24.16, 9) * mm});
            skLineSegment(sketch, "E29.right", {"start": v(-7.76, 12) * mm, "end": v(-7.76, 9) * mm});
            skSolve(sketch);
        }
        {
            var Q0;
            Q0 = qSketchRegion(id + "F14", true);
            extrude(context, id + "F15", {"entities" : qUnion([Q0]), "depth" : 1 * mm, "offsetDistance" : 25 * mm});
        }
        {
            var Q0;
            Q0=makeQuery(id+"F15.opExtrude","CAP_EDGE",EDGE,{"disambiguationData":[OSD([sQuery(id+"F14.wireOp",EDGE,"E29.bottom")])],"isStart":false});
            fillet(context, id + "F16", {"entities" : qUnion([Q0]), "radius" : 1 * mm, "tangentPropagation" : true, "allowEdgeOverflow" : false});
        }
        {
            var Q0;
            Q0=makeQuery(id+"F15.opExtrude","CAP_EDGE",EDGE,{"disambiguationData":[OSD([sQuery(id+"F14.wireOp",EDGE,"E29.top")])],"isStart":false});
            fillet(context, id + "F17", {"entities" : qUnion([Q0]), "radius" : 0.5 * mm, "tangentPropagation" : true, "allowEdgeOverflow" : false});
        }
        {
            var Q0;
            Q0=makeQuery(id+"F8.opExtrude","CAP_EDGE",EDGE,{"disambiguationData":[OSD([sQuery(id+"F0.wireOp",EDGE,"E16"),sQuery(id+"F0.wireOp",EDGE,"E17"),sQuery(id+"F0.wireOp",EDGE,"E18")])],"isStart":false});
            fillet(context, id + "F18", {"entities" : qUnion([Q0]), "radius" : 5 * mm, "tangentPropagation" : true, "allowEdgeOverflow" : false});
        }
        {
            var Q0;
            Q0=makeQuery(id+"F3.opExtrude","CAP_EDGE",EDGE,{"disambiguationData":[OSD([sQuery(id+"F0.wireOp",EDGE,"E26")])],"isStart":false});
            fillet(context, id + "F19", {"entities" : qUnion([Q0]), "radius" : 1.25 * mm, "tangentPropagation" : true, "allowEdgeOverflow" : false});
        }
    });
